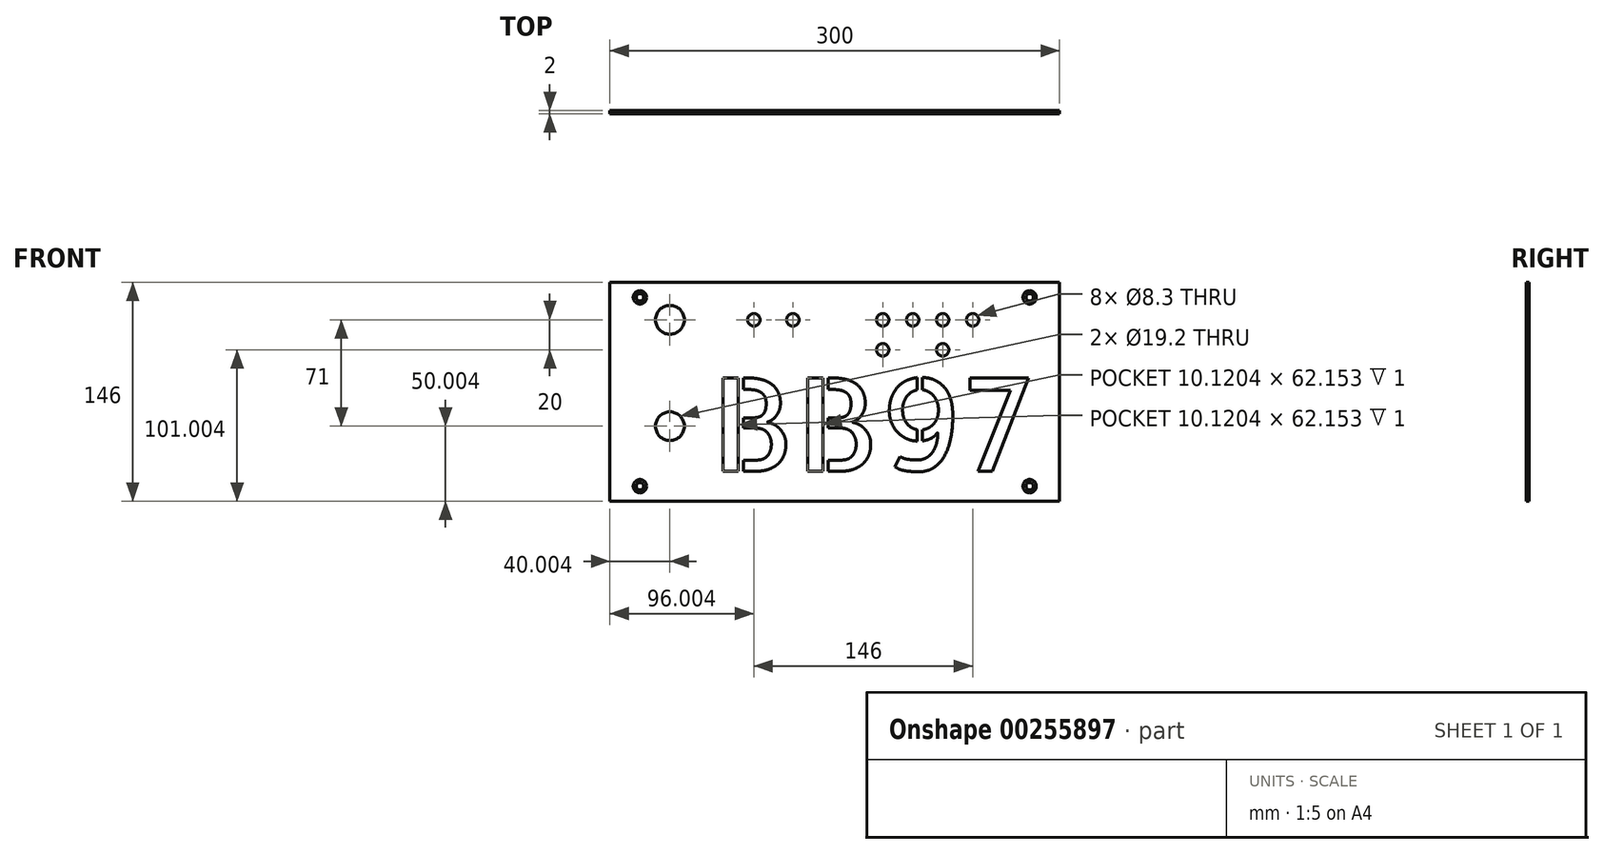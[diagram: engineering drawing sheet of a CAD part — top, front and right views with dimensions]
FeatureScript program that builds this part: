
annotation { "Feature Type Name" : "Feature", "Feature Type Description" : "" }
export const myFeature = defineFeature(function(context is Context, id is Id, definition is map)
    precondition{}
    {
        {
            var Q0;
            Q0=qCreatedBy(makeId("Front.planeOp"),FACE);
            var sketch = newSketch(context, id + "F0", { "sketchPlane" : qUnion([Q0])});
            skLineSegment(sketch, "E0.bottom", {"start": v(-140.42, 71.1) * mm, "end": v(159.58, 71.1) * mm});
            skLineSegment(sketch, "E0.top", {"start": v(-140.42, -74.9) * mm, "end": v(159.58, -74.9) * mm});
            skLineSegment(sketch, "E0.left", {"start": v(-140.42, 71.1) * mm, "end": v(-140.42, -74.9) * mm});
            skLineSegment(sketch, "E0.right", {"start": v(159.58, 71.1) * mm, "end": v(159.58, -74.9) * mm});
            skPoint(sketch, "E1", {"position": v(-120.42, -64.9) * mm});
            skPoint(sketch, "E2", {"position": v(139.58, -64.9) * mm});
            skCircle(sketch, "E3", {"center": v(-100.42, 46.1) * mm, "radius": 9.6 * mm});
            skCircle(sketch, "E4", {"center": v(-100.42, -24.9) * mm, "radius": 9.6 * mm});
            skCircle(sketch, "E5", {"center": v(-18.42, 46.1) * mm, "radius": 4.15 * mm});
            skCircle(sketch, "E6", {"center": v(-44.42, 46.1) * mm, "radius": 4.15 * mm});
            skCircle(sketch, "E7", {"center": v(41.58, 46.1) * mm, "radius": 4.15 * mm});
            skCircle(sketch, "E8", {"center": v(81.58, 46.1) * mm, "radius": 4.15 * mm});
            skCircle(sketch, "E9", {"center": v(101.58, 46.1) * mm, "radius": 4.15 * mm});
            skCircle(sketch, "E10", {"center": v(61.58, 46.1) * mm, "radius": 4.15 * mm});
            skText(sketch, "E11", { "text": "BB97", "fontName": "AllertaStencil-Regular.ttf"});
            skLineSegment(sketch, "E12", {"start": v(-140.42, 46.1) * mm, "end": v(159.58, 46.1) * mm, "construction": true});
            skPoint(sketch, "E13", {"position": v(41.58, 26.1) * mm});
            skPoint(sketch, "E14", {"position": v(81.58, 26.1) * mm});
            skCircle(sketch, "E15", {"center": v(41.58, 26.1) * mm, "radius": 4.15 * mm});
            skCircle(sketch, "E16", {"center": v(81.58, 26.1) * mm, "radius": 4.15 * mm});
            skPoint(sketch, "E17", {"position": v(-120.42, 61.1) * mm});
            skPoint(sketch, "E18", {"position": v(139.58, 61.1) * mm});
            const initialGuessF0  = {"E11": [-0.07314, -0.0549, 1, 0, 0.06218]};
            skSetInitialGuess(sketch, initialGuessF0);
            skSolve(sketch);
        }
        {
            var Q0;
            Q0=makeQuery(id+"F0.imprint","IMPRINT",FACE,{"disambiguationData":[TD([[makeQuery(id+"F0.imprint","IMPRINT",EDGE,{"derivedFrom":sQuery(id+"F0.wireOp",EDGE,"E0.bottom")}),-1.0]])]});
            var Q1;
            Q1=makeQuery(id+"F0.imprint","IMPRINT",FACE,{"disambiguationData":[TD([[makeQuery(id+"F0.imprint","IMPRINT",EDGE,{"derivedFrom":sQuery(id+"F0.wireOp",EDGE,"E11.sketch_text.stroke-39")}),-1.0]])]});
            var Q2;
            Q2=makeQuery(id+"F0.imprint","IMPRINT",FACE,{"disambiguationData":[TD([[makeQuery(id+"F0.imprint","IMPRINT",EDGE,{"derivedFrom":sQuery(id+"F0.wireOp",EDGE,"E11.sketch_text.stroke-0")}),-1.0]])]});
            var Q3;
            Q3=makeQuery(id+"F0.imprint","IMPRINT",FACE,{"disambiguationData":[TD([[makeQuery(id+"F0.imprint","IMPRINT",EDGE,{"derivedFrom":sQuery(id+"F0.wireOp",EDGE,"E11.sketch_text.stroke-82")}),-1.0]])]});
            var Q4;
            Q4=makeQuery(id+"F0.imprint","IMPRINT",FACE,{"disambiguationData":[TD([[makeQuery(id+"F0.imprint","IMPRINT",EDGE,{"derivedFrom":sQuery(id+"F0.wireOp",EDGE,"E11.sketch_text.stroke-43")}),-1.0]])]});
            var Q5;
            Q5=makeQuery(id+"F0.imprint","IMPRINT",FACE,{"disambiguationData":[TD([[makeQuery(id+"F0.imprint","IMPRINT",EDGE,{"derivedFrom":sQuery(id+"F0.wireOp",EDGE,"E11.sketch_text.stroke-86")}),-1.0]])]});
            var Q6;
            Q6=makeQuery(id+"F0.imprint","IMPRINT",FACE,{"disambiguationData":[TD([[makeQuery(id+"F0.imprint","IMPRINT",EDGE,{"derivedFrom":sQuery(id+"F0.wireOp",EDGE,"E11.sketch_text.stroke-100")}),-1.0]])]});
            var Q7;
            Q7=makeQuery(id+"F0.imprint","IMPRINT",FACE,{"disambiguationData":[TD([[makeQuery(id+"F0.imprint","IMPRINT",EDGE,{"derivedFrom":sQuery(id+"F0.wireOp",EDGE,"E11.sketch_text.stroke-131")}),-1.0]])]});
            extrude(context, id + "F1", {"entities" : qUnion([Q0, Q1, Q2, Q3, Q4, Q5, Q6, Q7]), "oppositeDirection" : true, "depth" : 2 * mm});
        }
        {
            var Q0;
            Q0=makeQuery(id+"F0.imprint","IMPRINT",FACE,{"disambiguationData":[TD([[makeQuery(id+"F0.imprint","IMPRINT",EDGE,{"derivedFrom":sQuery(id+"F0.wireOp",EDGE,"E11.sketch_text.stroke-86")}),-1.0]])]});
            var Q1;
            Q1=makeQuery(id+"F0.imprint","IMPRINT",FACE,{"disambiguationData":[TD([[makeQuery(id+"F0.imprint","IMPRINT",EDGE,{"derivedFrom":sQuery(id+"F0.wireOp",EDGE,"E11.sketch_text.stroke-43")}),-1.0]])]});
            var Q2;
            Q2=makeQuery(id+"F0.imprint","IMPRINT",FACE,{"disambiguationData":[TD([[makeQuery(id+"F0.imprint","IMPRINT",EDGE,{"derivedFrom":sQuery(id+"F0.wireOp",EDGE,"E11.sketch_text.stroke-82")}),-1.0]])]});
            var Q3;
            Q3=makeQuery(id+"F0.imprint","IMPRINT",FACE,{"disambiguationData":[TD([[makeQuery(id+"F0.imprint","IMPRINT",EDGE,{"derivedFrom":sQuery(id+"F0.wireOp",EDGE,"E11.sketch_text.stroke-0")}),-1.0]])]});
            var Q4;
            Q4=makeQuery(id+"F0.imprint","IMPRINT",FACE,{"disambiguationData":[TD([[makeQuery(id+"F0.imprint","IMPRINT",EDGE,{"derivedFrom":sQuery(id+"F0.wireOp",EDGE,"E11.sketch_text.stroke-39")}),-1.0]])]});
            var Q5;
            Q5=makeQuery(id+"F0.imprint","IMPRINT",FACE,{"disambiguationData":[TD([[makeQuery(id+"F0.imprint","IMPRINT",EDGE,{"derivedFrom":sQuery(id+"F0.wireOp",EDGE,"E11.sketch_text.stroke-100")}),-1.0]])]});
            var Q6;
            Q6=makeQuery(id+"F0.imprint","IMPRINT",FACE,{"disambiguationData":[TD([[makeQuery(id+"F0.imprint","IMPRINT",EDGE,{"derivedFrom":sQuery(id+"F0.wireOp",EDGE,"E11.sketch_text.stroke-131")}),-1.0]])]});
            extrude(context, id + "F2", {"entities" : qUnion([Q0, Q1, Q2, Q3, Q4, Q5, Q6]), "operationType" : NewBodyOperationType.REMOVE, "oppositeDirection" : true, "depth" : 1 * mm});
        }
        {
            var Q0;
            Q0=sQuery(id+"F0.wireOp",VERTEX,"E17");
            var Q1;
            Q1=sQuery(id+"F0.wireOp",VERTEX,"E1");
            var Q2;
            Q2=sQuery(id+"F0.wireOp",VERTEX,"E2");
            var Q3;
            Q3=sQuery(id+"F0.wireOp",VERTEX,"E18");
            var Q4;
            Q4=makeQuery(id+"F1.opExtrude","SWEPT_BODY",BODY,{"disambiguationData":[OSD([sQuery(id+"F0.wireOp",EDGE,"E0.bottom"),sQuery(id+"F0.wireOp",EDGE,"E0.top"),sQuery(id+"F0.wireOp",EDGE,"E0.left"),sQuery(id+"F0.wireOp",EDGE,"E0.right"),sQuery(id+"F0.wireOp",EDGE,"E3"),sQuery(id+"F0.wireOp",EDGE,"E4"),sQuery(id+"F0.wireOp",EDGE,"E5"),sQuery(id+"F0.wireOp",EDGE,"E6"),sQuery(id+"F0.wireOp",EDGE,"E7"),sQuery(id+"F0.wireOp",EDGE,"E8"),sQuery(id+"F0.wireOp",EDGE,"E9"),sQuery(id+"F0.wireOp",EDGE,"E10"),sQuery(id+"F0.wireOp",EDGE,"E15"),sQuery(id+"F0.wireOp",EDGE,"E16")])]});
            hole(context, id + "F3", {"style" : HoleStyle.C_SINK, "endStyle" : HoleEndStyle.THROUGH, "standardTappedOrClearance" : lookupTablePath({ "standard" : "ISO", "engagement" : "75%", "pitch" : "0.75 mm", "size" : "M4", "type" : "Tapped" }), "standardBlindInLast" : lookupTablePath({ "standard" : "ISO", "engagement" : "75%", "pitch" : "0.75 mm", "size" : "M4", "type" : "Tapped" }), "holeDiameter" : 3.2 * mm, "cSinkDiameter" : 8.96 * mm, "cSinkAngle" : 90 * degree, "showTappedDepth" : true, "tappedDepth" : 12 * mm, "tapClearance" : 3, "startFromSketch" : true, "locations" : qUnion([Q0, Q1, Q2, Q3]), "scope" : qUnion([Q4])});
        }
    });
